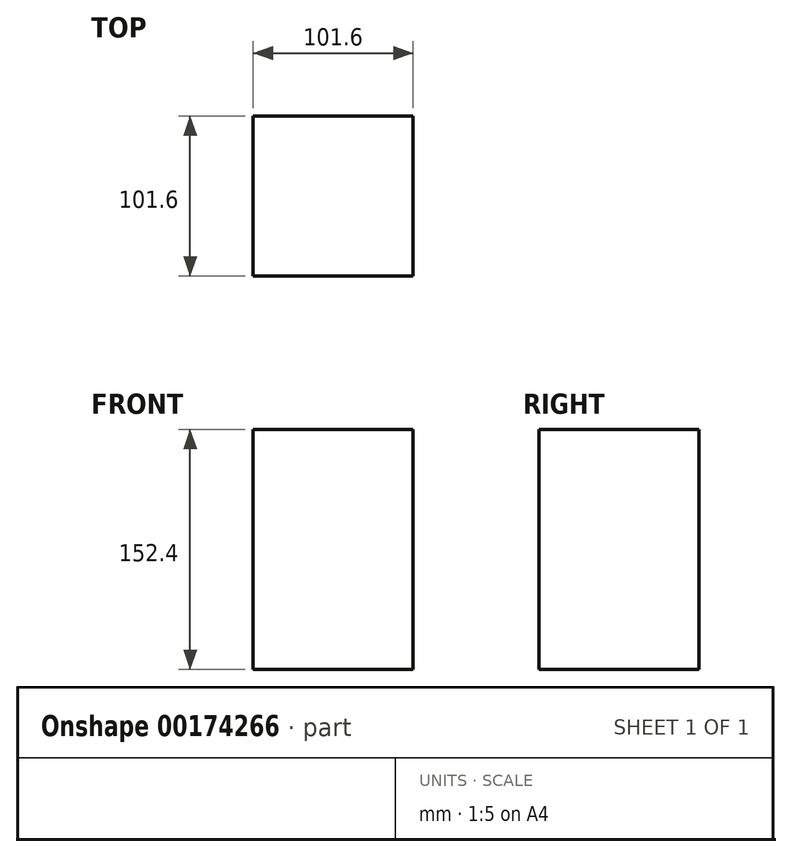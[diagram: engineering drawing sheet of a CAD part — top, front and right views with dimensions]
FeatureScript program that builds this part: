
annotation { "Feature Type Name" : "Feature", "Feature Type Description" : "" }
export const myFeature = defineFeature(function(context is Context, id is Id, definition is map)
    precondition{}
    {
        {
            var Q0;
            Q0=qCreatedBy(makeId("Top.planeOp"),FACE);
            var sketch = newSketch(context, id + "F0", { "sketchPlane" : qUnion([Q0])});
            skLineSegment(sketch, "E0.bottom", {"start": v(50.8, -50.8) * mm, "end": v(-50.8, -50.8) * mm});
            skLineSegment(sketch, "E0.top", {"start": v(50.8, 50.8) * mm, "end": v(-50.8, 50.8) * mm});
            skLineSegment(sketch, "E0.left", {"start": v(50.8, -50.8) * mm, "end": v(50.8, 50.8) * mm});
            skLineSegment(sketch, "E0.right", {"start": v(-50.8, -50.8) * mm, "end": v(-50.8, 50.8) * mm});
            skPoint(sketch, "E0.middle", {"position": v(0, 0) * mm});
            skSolve(sketch);
        }
        {
            var Q0;
            Q0=qCreatedBy(makeId("Top.planeOp"),FACE);
            cPlane(context, id + "F1", {"entities" : qUnion([Q0]), "cplaneType" : CPlaneType.OFFSET, "offset" : 152.4 * mm, "width" : 152.4 * mm, "height" : 152.4 * mm});
        }
        {
            var Q0;
            Q0=qCreatedBy(id+"F1.planeOp",FACE);
            var sketch = newSketch(context, id + "F2", { "sketchPlane" : qUnion([Q0])});
            skLineSegment(sketch, "E1.bottom", {"start": v(-50.8, 50.8) * mm, "end": v(50.8, 50.8) * mm});
            skLineSegment(sketch, "E1.top", {"start": v(-50.8, -50.8) * mm, "end": v(50.8, -50.8) * mm});
            skLineSegment(sketch, "E1.left", {"start": v(-50.8, 50.8) * mm, "end": v(-50.8, -50.8) * mm});
            skLineSegment(sketch, "E1.right", {"start": v(50.8, 50.8) * mm, "end": v(50.8, -50.8) * mm});
            skSolve(sketch);
        }
        {
            var Q0;
            Q0=makeQuery(id+"F2.imprint","IMPRINT",FACE,{"disambiguationData":[TD([[makeQuery(id+"F2.imprint","IMPRINT",EDGE,{"derivedFrom":sQuery(id+"F2.wireOp",EDGE,"E1.bottom")}),-1.0]])]});
            var Q1;
            Q1=makeQuery(id+"F0.imprint","IMPRINT",FACE,{"disambiguationData":[TD([[makeQuery(id+"F0.imprint","IMPRINT",EDGE,{"derivedFrom":sQuery(id+"F0.wireOp",EDGE,"E0.bottom")}),-1.0]])]});
            loft(context, id + "F3", {"sheetProfilesArray" : [{ "sheetProfileEntities" : qUnion([Q0]) }, { "sheetProfileEntities" : qUnion([Q1]) }]});
        }
    });
